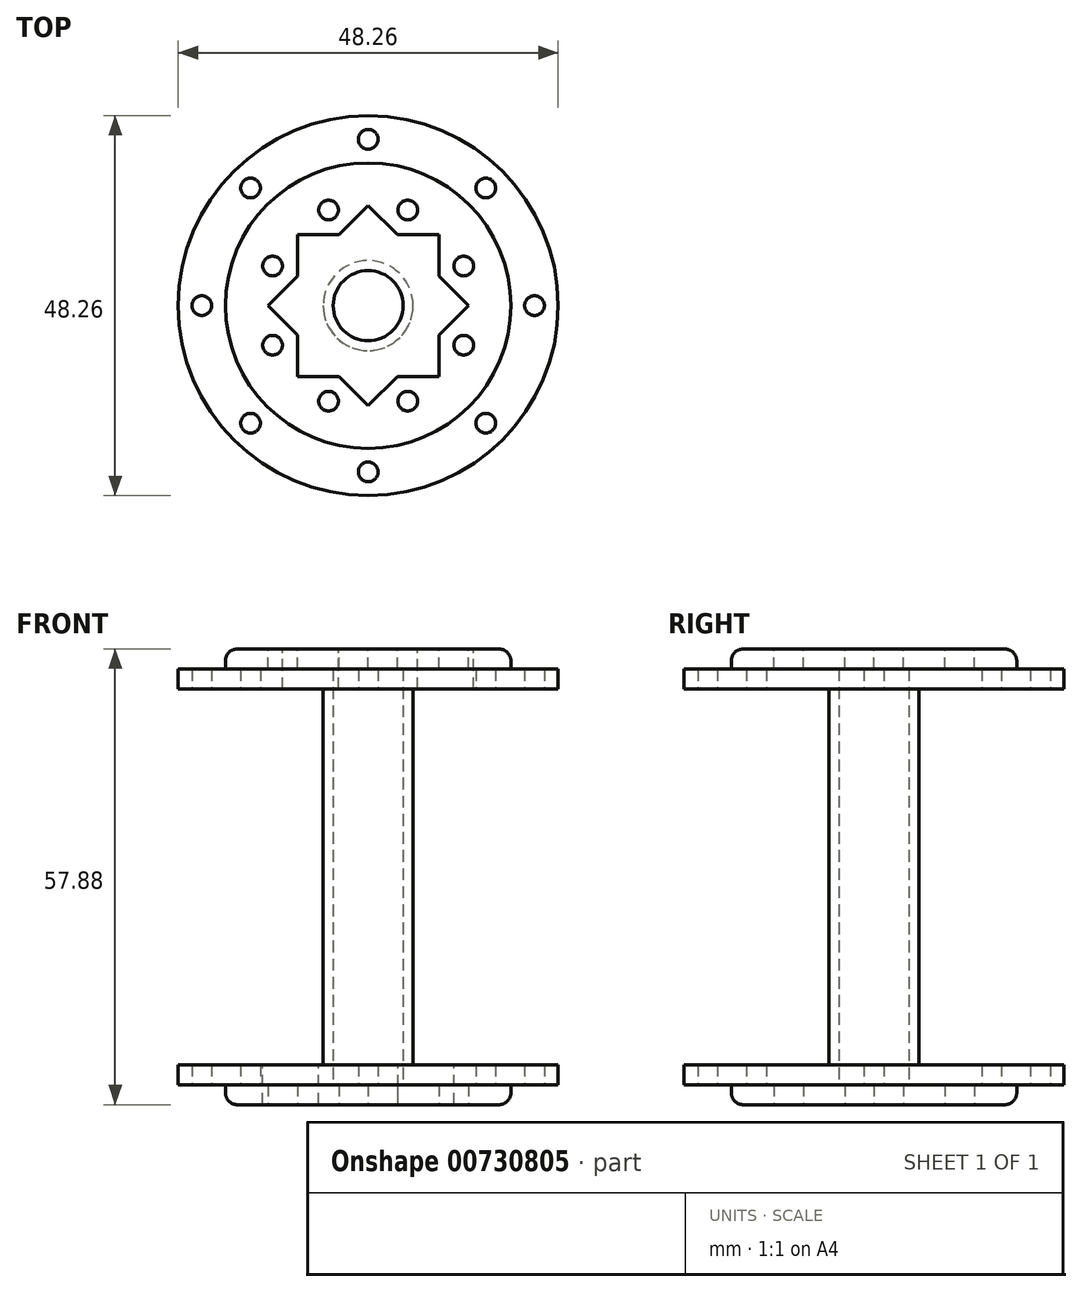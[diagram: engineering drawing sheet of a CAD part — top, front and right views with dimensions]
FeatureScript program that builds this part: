
annotation { "Feature Type Name" : "Feature", "Feature Type Description" : "" }
export const myFeature = defineFeature(function(context is Context, id is Id, definition is map)
    precondition{}
    {
        {
            var Q0;
            Q0=qCreatedBy(makeId("Top.planeOp"),FACE);
            var sketch = newSketch(context, id + "F0", { "sketchPlane" : qUnion([Q0])});
            skCircle(sketch, "E0", {"center": v(0, 0) * mm, "radius": 5.71 * mm});
            skCircle(sketch, "E1", {"center": v(0, 0) * mm, "radius": 4.45 * mm});
            skSolve(sketch);
        }
        {
            var Q0;
            Q0=makeQuery(id+"F0.imprint","IMPRINT",FACE,{"disambiguationData":[TD([[makeQuery(id+"F0.imprint","IMPRINT",EDGE,{"derivedFrom":sQuery(id+"F0.wireOp",EDGE,"E0")}),1.0]])]});
            extrude(context, id + "F1", {"entities" : qUnion([Q0]), "depth" : (45.72 + 2.54 + 2 + 2.54) * mm, "offsetDistance" : 25 * mm});
        }
        {
            var Q0;
            Q0=makeQuery(id+"F1.opExtrude","CAP_FACE",FACE,{"disambiguationData":[OSD([sQuery(id+"F0.wireOp",EDGE,"E0"),sQuery(id+"F0.wireOp",EDGE,"E1")])],"isStart":false});
            var sketch = newSketch(context, id + "F2", { "sketchPlane" : qUnion([Q0])});
            skCircle(sketch, "E2", {"center": v(0, 0) * mm, "radius": 24.13 * mm});
            skCircle(sketch, "E3", {"center": v(0, 0) * mm, "radius": 5.71 * mm});
            skSolve(sketch);
        }
        {
            var Q0;
            Q0=makeQuery(id+"F2.imprint","IMPRINT",FACE,{"disambiguationData":[TD([[makeQuery(id+"F2.imprint","IMPRINT",EDGE,{"derivedFrom":sQuery(id+"F2.wireOp",EDGE,"E2")}),1.0]])]});
            extrude(context, id + "F3", {"entities" : qUnion([Q0]), "operationType" : NewBodyOperationType.ADD, "oppositeDirection" : true, "depth" : 2.54 * mm, "offsetDistance" : 25 * mm});
        }
        {
            var Q0;
            Q0=makeQuery(id+"F1.opExtrude","CAP_FACE",FACE,{"disambiguationData":[OSD([sQuery(id+"F0.wireOp",EDGE,"E0"),sQuery(id+"F0.wireOp",EDGE,"E1")])],"isStart":true});
            var sketch = newSketch(context, id + "F4", { "sketchPlane" : qUnion([Q0])});
            skCircle(sketch, "E4", {"center": v(0, 0) * mm, "radius": 5.71 * mm});
            skCircle(sketch, "E5", {"center": v(0, 0) * mm, "radius": 24.13 * mm});
            skSolve(sketch);
        }
        {
            var Q0;
            Q0 = qSketchRegion(id + "F4", true);
            extrude(context, id + "F5", {"entities" : qUnion([Q0]), "operationType" : NewBodyOperationType.ADD, "oppositeDirection" : true, "depth" : 2.54 * mm, "offsetDistance" : 25 * mm});
        }
        {
            var Q0;
            Q0=makeQuery(id+"F5.boolean.opBoolean","MERGE",FACE,{"derivedFrom":[makeQuery(id+"F1.opExtrude","CAP_FACE",FACE,{"disambiguationData":[OSD([sQuery(id+"F0.wireOp",EDGE,"E0"),sQuery(id+"F0.wireOp",EDGE,"E1")])],"isStart":true}),makeQuery(id+"F5.opExtrude","CAP_FACE",FACE,{"disambiguationData":[OSD([sQuery(id+"F4.wireOp",EDGE,"E4"),sQuery(id+"F4.wireOp",EDGE,"E5")])],"isStart":true})]});
            var sketch = newSketch(context, id + "F6", { "sketchPlane" : qUnion([Q0])});
            skCircle(sketch, "E6", {"center": v(-21.13, 0) * mm, "radius": 1.25 * mm});
            skCircle(sketch, "E7.1.0", {"center": v(-14.94, -14.94) * mm, "radius": 1.25 * mm});
            skCircle(sketch, "E7.2.0", {"center": v(0, -21.13) * mm, "radius": 1.25 * mm});
            skCircle(sketch, "E7.3.0", {"center": v(14.94, -14.94) * mm, "radius": 1.25 * mm});
            skCircle(sketch, "E7.4.0", {"center": v(21.13, 0) * mm, "radius": 1.25 * mm});
            skCircle(sketch, "E7.5.0", {"center": v(14.94, 14.94) * mm, "radius": 1.25 * mm});
            skCircle(sketch, "E7.6.0", {"center": v(0, 21.13) * mm, "radius": 1.25 * mm});
            skCircle(sketch, "E7.7.0", {"center": v(-14.94, 14.94) * mm, "radius": 1.25 * mm});
            skPoint(sketch, "E7.center", {"position": v(0, 0) * mm});
            skSolve(sketch);
        }
        {
            var Q0;
            Q0 = qSketchRegion(id + "F6", true);
            extrude(context, id + "F7", {"entities" : qUnion([Q0]), "operationType" : NewBodyOperationType.REMOVE, "endBound" : BoundingType.THROUGH_ALL, "oppositeDirection" : true, "depth" : 2.54 * mm, "offsetDistance" : 25 * mm});
        }
        {
            var Q0;
            Q0=makeQuery(id+"F5.boolean.opBoolean","MERGE",FACE,{"derivedFrom":[makeQuery(id+"F1.opExtrude","CAP_FACE",FACE,{"disambiguationData":[OSD([sQuery(id+"F0.wireOp",EDGE,"E0"),sQuery(id+"F0.wireOp",EDGE,"E1")])],"isStart":true}),makeQuery(id+"F5.opExtrude","CAP_FACE",FACE,{"disambiguationData":[OSD([sQuery(id+"F4.wireOp",EDGE,"E4"),sQuery(id+"F4.wireOp",EDGE,"E5")])],"isStart":true})]});
            var sketch = newSketch(context, id + "F8", { "sketchPlane" : qUnion([Q0])});
            skCircle(sketch, "E8", {"center": v(0, 0) * mm, "radius": 18.13 * mm});
            skCircle(sketch, "E9", {"center": v(0, 0) * mm, "radius": 4.45 * mm});
            skSolve(sketch);
        }
        {
            var Q0;
            Q0 = qSketchRegion(id + "F8", true);
            extrude(context, id + "F9", {"entities" : qUnion([Q0]), "operationType" : NewBodyOperationType.ADD, "depth" : 2.54 * mm, "offsetDistance" : 25 * mm});
        }
        {
            var Q0;
            Q0=makeQuery(id+"F9.opExtrude","CAP_EDGE",EDGE,{"disambiguationData":[OSD([sQuery(id+"F8.wireOp",EDGE,"E8")])],"isStart":false});
            fillet(context, id + "F10", {"entities" : qUnion([Q0]), "radius" : 1.5 * mm, "tangentPropagation" : true, "allowEdgeOverflow" : false});
        }
        {
            var Q0;
            Q0=makeQuery(id+"F9.opExtrude","CAP_FACE",FACE,{"disambiguationData":[OSD([sQuery(id+"F8.wireOp",EDGE,"E8"),sQuery(id+"F8.wireOp",EDGE,"E9")])],"isStart":false});
            var sketch = newSketch(context, id + "F11", { "sketchPlane" : qUnion([Q0])});
            skLineSegment(sketch, "E10", {"start": v(0, 12.73) * mm, "end": v(-3.73, 9) * mm});
            skLineSegment(sketch, "E11", {"start": v(3.73, 9) * mm, "end": v(0, 12.73) * mm});
            skLineSegment(sketch, "E12.1.0", {"start": v(-3.73, 9) * mm, "end": v(-9, 9) * mm});
            skLineSegment(sketch, "E12.1.1", {"start": v(-9, 9) * mm, "end": v(-9, 3.73) * mm});
            skLineSegment(sketch, "E12.2.0", {"start": v(-9, 3.73) * mm, "end": v(-12.73, 0) * mm});
            skLineSegment(sketch, "E12.2.1", {"start": v(-12.73, 0) * mm, "end": v(-9, -3.73) * mm});
            skLineSegment(sketch, "E12.3.0", {"start": v(-9, -3.73) * mm, "end": v(-9, -9) * mm});
            skLineSegment(sketch, "E12.3.1", {"start": v(-9, -9) * mm, "end": v(-3.73, -9) * mm});
            skPoint(sketch, "E12.center", {"position": v(0, 0) * mm});
            skLineSegment(sketch, "E13.1.4.0", {"start": v(-3.73, -9) * mm, "end": v(0, -12.73) * mm});
            skLineSegment(sketch, "E13.3.4.0", {"start": v(0, -12.73) * mm, "end": v(3.73, -9) * mm});
            skLineSegment(sketch, "E13.1.5.0", {"start": v(3.73, -9) * mm, "end": v(9, -9) * mm});
            skLineSegment(sketch, "E13.3.5.0", {"start": v(9, -9) * mm, "end": v(9, -3.73) * mm});
            skLineSegment(sketch, "E13.1.6.0", {"start": v(9, -3.73) * mm, "end": v(12.73, 0) * mm});
            skLineSegment(sketch, "E13.3.6.0", {"start": v(12.73, 0) * mm, "end": v(9, 3.73) * mm});
            skLineSegment(sketch, "E13.1.7.0", {"start": v(9, 3.73) * mm, "end": v(9, 9) * mm});
            skLineSegment(sketch, "E13.3.7.0", {"start": v(9, 9) * mm, "end": v(3.73, 9) * mm});
            skSolve(sketch);
        }
        {
            var Q0;
            Q0=makeQuery(id+"F11.imprint","IMPRINT",FACE,{"disambiguationData":[TD([[makeQuery(id+"F11.imprint","IMPRINT",EDGE,{"derivedFrom":makeQuery(id+"F9.opExtrude","CAP_EDGE",EDGE,{"disambiguationData":[OSD([sQuery(id+"F8.wireOp",EDGE,"E9")])],"isStart":false})}),-1.0]])]});
            var Q1;
            Q1=makeQuery(id+"F11.imprint","IMPRINT",FACE,{"disambiguationData":[TD([[makeQuery(id+"F11.imprint","IMPRINT",EDGE,{"derivedFrom":makeQuery(id+"F9.opExtrude","CAP_EDGE",EDGE,{"disambiguationData":[OSD([sQuery(id+"F8.wireOp",EDGE,"E9")])],"isStart":false})}),1.0]])]});
            extrude(context, id + "F12", {"entities" : qUnion([Q0, Q1]), "operationType" : NewBodyOperationType.REMOVE, "oppositeDirection" : true, "depth" : 2.54 * mm, "offsetDistance" : 25 * mm});
        }
        {
            var Q0;
            Q0=makeQuery(id+"F3.boolean.opBoolean","MERGE",FACE,{"derivedFrom":[makeQuery(id+"F1.opExtrude","CAP_FACE",FACE,{"disambiguationData":[OSD([sQuery(id+"F0.wireOp",EDGE,"E0"),sQuery(id+"F0.wireOp",EDGE,"E1")])],"isStart":false}),makeQuery(id+"F3.opExtrude","CAP_FACE",FACE,{"disambiguationData":[OSD([sQuery(id+"F2.wireOp",EDGE,"E2"),sQuery(id+"F2.wireOp",EDGE,"E3")])],"isStart":true})]});
            var sketch = newSketch(context, id + "F13", { "sketchPlane" : qUnion([Q0])});
            skCircle(sketch, "E14", {"center": v(0, 0) * mm, "radius": 18.13 * mm});
            skCircle(sketch, "E15", {"center": v(0, 0) * mm, "radius": 4.45 * mm});
            skSolve(sketch);
        }
        {
            var Q0;
            Q0 = qSketchRegion(id + "F13", true);
            extrude(context, id + "F14", {"entities" : qUnion([Q0]), "operationType" : NewBodyOperationType.ADD, "depth" : 2.54 * mm, "offsetDistance" : 25 * mm});
        }
        {
            var Q0;
            Q0=makeQuery(id+"F14.opExtrude","CAP_EDGE",EDGE,{"disambiguationData":[OSD([sQuery(id+"F13.wireOp",EDGE,"E14")])],"isStart":false});
            fillet(context, id + "F15", {"entities" : qUnion([Q0]), "radius" : 1.5 * mm, "tangentPropagation" : true, "allowEdgeOverflow" : false});
        }
        {
            var Q0;
            Q0=makeQuery(id+"F14.opExtrude","CAP_FACE",FACE,{"disambiguationData":[OSD([sQuery(id+"F13.wireOp",EDGE,"E14"),sQuery(id+"F13.wireOp",EDGE,"E15")])],"isStart":false});
            var sketch = newSketch(context, id + "F16", { "sketchPlane" : qUnion([Q0])});
            skLineSegment(sketch, "E16", {"start": v(0, 12.73) * mm, "end": v(-3.73, 9) * mm});
            skLineSegment(sketch, "E17", {"start": v(3.73, 9) * mm, "end": v(0, 12.73) * mm});
            skLineSegment(sketch, "E18.1.0", {"start": v(-3.73, 9) * mm, "end": v(-9, 9) * mm});
            skLineSegment(sketch, "E18.1.1", {"start": v(-9, 9) * mm, "end": v(-9, 3.73) * mm});
            skLineSegment(sketch, "E18.2.0", {"start": v(-9, 3.73) * mm, "end": v(-12.73, 0) * mm});
            skLineSegment(sketch, "E18.2.1", {"start": v(-12.73, 0) * mm, "end": v(-9, -3.73) * mm});
            skLineSegment(sketch, "E18.3.0", {"start": v(-9, -3.73) * mm, "end": v(-9, -9) * mm});
            skLineSegment(sketch, "E18.3.1", {"start": v(-9, -9) * mm, "end": v(-3.73, -9) * mm});
            skLineSegment(sketch, "E18.4.0", {"start": v(-3.73, -9) * mm, "end": v(0, -12.73) * mm});
            skLineSegment(sketch, "E18.4.1", {"start": v(0, -12.73) * mm, "end": v(3.73, -9) * mm});
            skLineSegment(sketch, "E18.5.0", {"start": v(3.73, -9) * mm, "end": v(9, -9) * mm});
            skLineSegment(sketch, "E18.5.1", {"start": v(9, -9) * mm, "end": v(9, -3.73) * mm});
            skLineSegment(sketch, "E18.6.0", {"start": v(9, -3.73) * mm, "end": v(12.73, 0) * mm});
            skLineSegment(sketch, "E18.6.1", {"start": v(12.73, 0) * mm, "end": v(9, 3.73) * mm});
            skLineSegment(sketch, "E18.7.0", {"start": v(9, 3.73) * mm, "end": v(9, 9) * mm});
            skLineSegment(sketch, "E18.7.1", {"start": v(9, 9) * mm, "end": v(3.73, 9) * mm});
            skPoint(sketch, "E18.center", {"position": v(0, 0) * mm});
            skCircle(sketch, "E19", {"center": v(0, 0) * mm, "radius": 4.45 * mm});
            skSolve(sketch);
        }
        {
            var Q0;
            Q0 = qSketchRegion(id + "F16", true);
            extrude(context, id + "F17", {"entities" : qUnion([Q0]), "operationType" : NewBodyOperationType.REMOVE, "oppositeDirection" : true, "depth" : 2.54 * mm, "offsetDistance" : 25 * mm});
        }
        {
            var Q0;
            Q0=makeQuery(id+"F14.opExtrude","CAP_FACE",FACE,{"disambiguationData":[OSD([sQuery(id+"F13.wireOp",EDGE,"E14"),sQuery(id+"F13.wireOp",EDGE,"E15")])],"isStart":false});
            var sketch = newSketch(context, id + "F18", { "sketchPlane" : qUnion([Q0])});
            skCircle(sketch, "E20", {"center": v(-12.14, 5.03) * mm, "radius": 1.25 * mm});
            skCircle(sketch, "E21.1.0", {"center": v(-12.14, -5.03) * mm, "radius": 1.25 * mm});
            skCircle(sketch, "E21.2.0", {"center": v(-5.03, -12.14) * mm, "radius": 1.25 * mm});
            skCircle(sketch, "E21.3.0", {"center": v(5.03, -12.14) * mm, "radius": 1.25 * mm});
            skCircle(sketch, "E21.4.0", {"center": v(12.14, -5.03) * mm, "radius": 1.25 * mm});
            skCircle(sketch, "E21.5.0", {"center": v(12.14, 5.03) * mm, "radius": 1.25 * mm});
            skCircle(sketch, "E21.6.0", {"center": v(5.03, 12.14) * mm, "radius": 1.25 * mm});
            skCircle(sketch, "E21.7.0", {"center": v(-5.03, 12.14) * mm, "radius": 1.25 * mm});
            skPoint(sketch, "E21.center", {"position": v(0, 0) * mm});
            skSolve(sketch);
        }
        {
            var Q0;
            Q0 = qSketchRegion(id + "F18", true);
            extrude(context, id + "F19", {"entities" : qUnion([Q0]), "operationType" : NewBodyOperationType.REMOVE, "endBound" : BoundingType.THROUGH_ALL, "oppositeDirection" : true, "depth" : (2.54 * 2) * mm, "offsetDistance" : 25 * mm});
        }
    });
